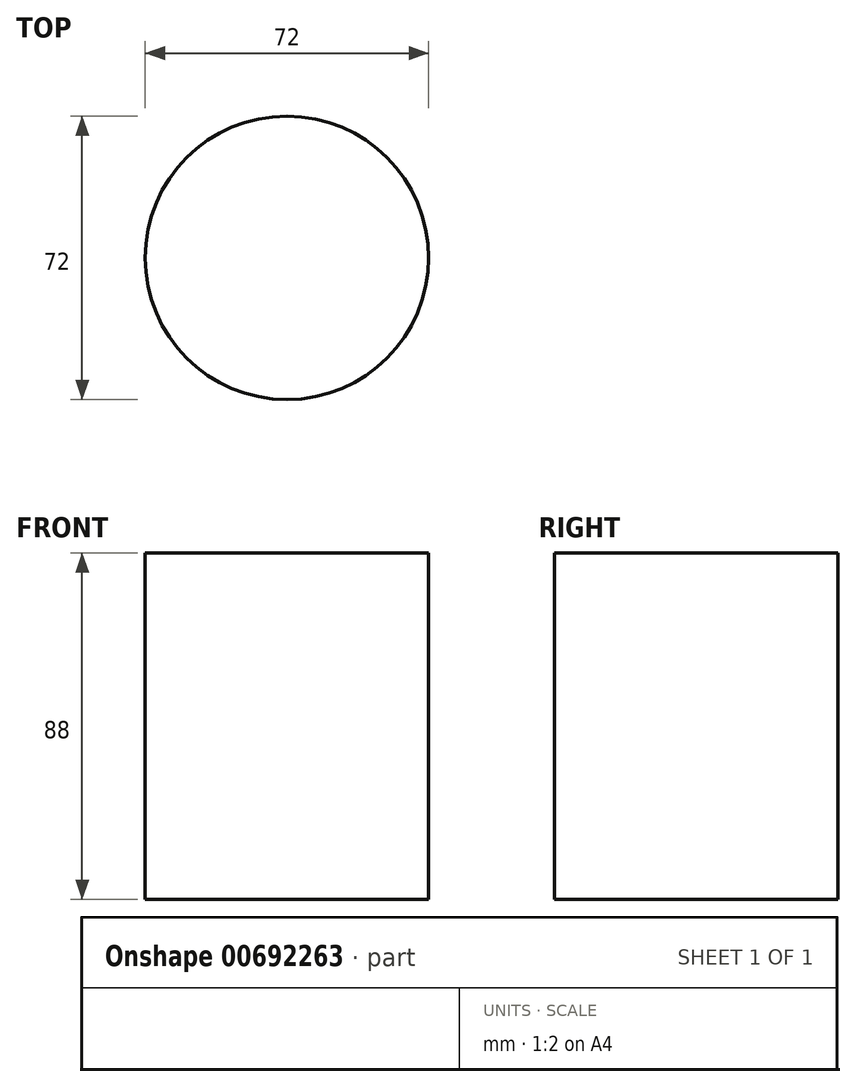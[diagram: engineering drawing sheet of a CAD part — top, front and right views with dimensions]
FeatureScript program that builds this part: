
annotation { "Feature Type Name" : "Feature", "Feature Type Description" : "" }
export const myFeature = defineFeature(function(context is Context, id is Id, definition is map)
    precondition{}
    {
        {
            var Q0;
            Q0=qCreatedBy(makeId("Top.planeOp"),FACE);
            var sketch = newSketch(context, id + "F0", { "sketchPlane" : qUnion([Q0])});
            skCircle(sketch, "E0", {"center": v(0, 0) * mm, "radius": 36 * mm});
            skSolve(sketch);
        }
        {
            var Q0;
            Q0 = qSketchRegion(id + "F0", true);
            extrude(context, id + "F1", {"entities" : qUnion([Q0]), "depth" : 88 * mm, "offsetDistance" : 25 * mm});
        }
    });
